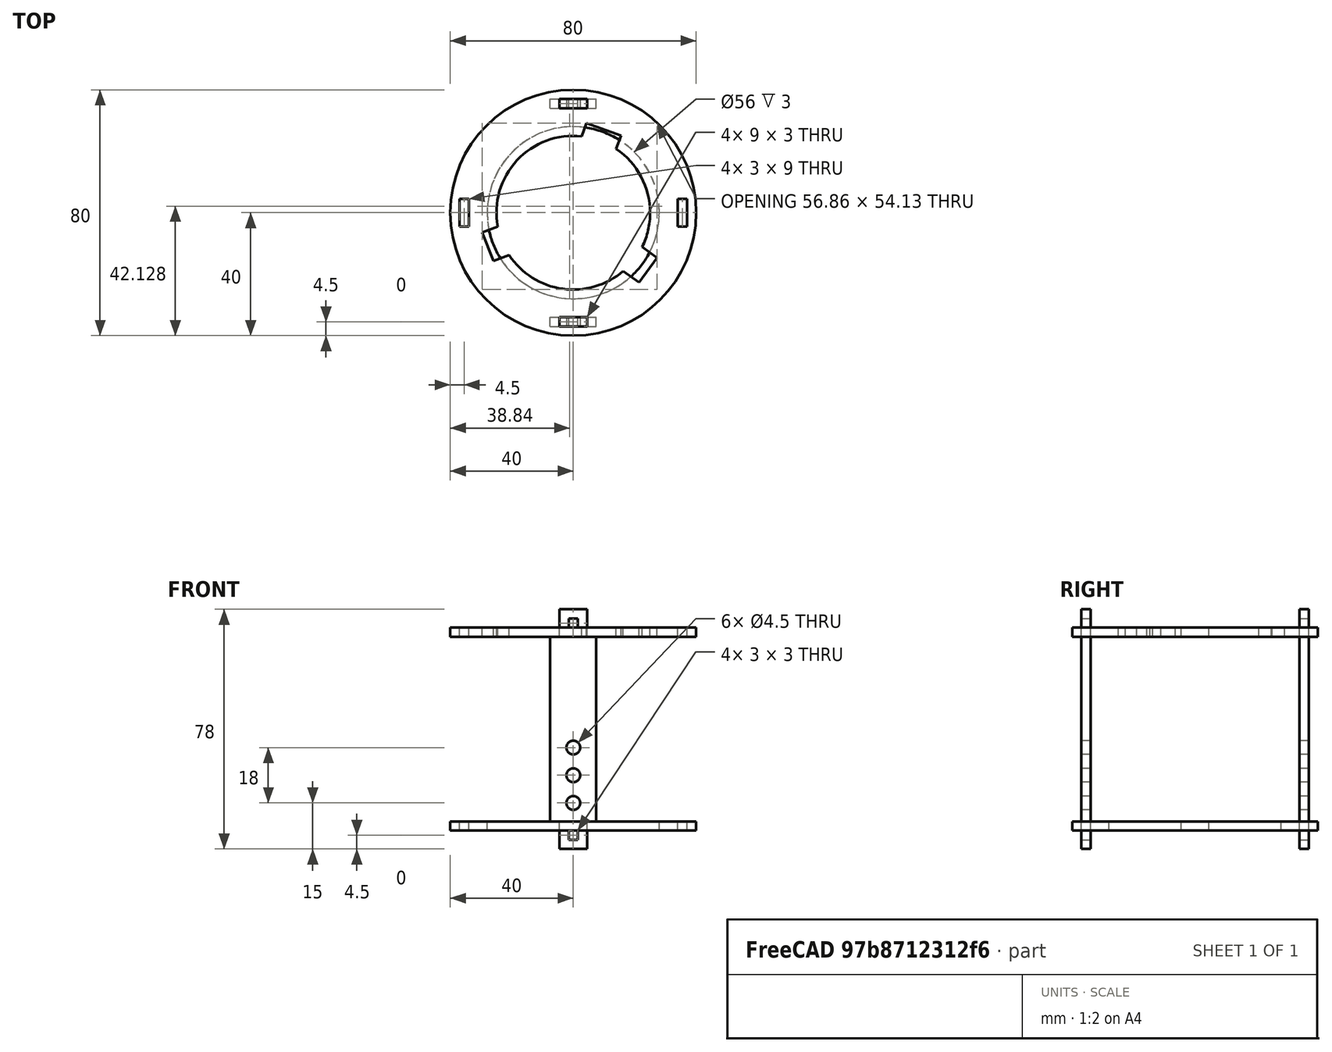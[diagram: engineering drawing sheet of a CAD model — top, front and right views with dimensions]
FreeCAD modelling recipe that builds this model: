
FCSTD DOCUMENT  (FreeCAD 0.16R6707 (Git))
Label: turretPitch
License: All rights reserved
LicenseURL: http://en.wikipedia.org/wiki/All_rights_reserved
objects: Part::Cut×23, Part::Box×21, Part::Cylinder×10, Part::MultiFuse×2
note: 56 computed .brp shape members not serialized (recipe doc carries the construction recipe); baked Part::Feature solids carry a one-line shape summary decoded from their .brp

FEATURE [Part::Cylinder] Cylinder
  Angle = 360
  Height = 3
  Radius = 40
FEATURE [Part::Cylinder] Cylinder001
  Angle = 360
  Height = 3
  Radius = 25
FEATURE [Part::Cut] Cut
  Base = -> Cylinder
  Tool = -> Cylinder001
FEATURE [Part::Box] Box  label="Cube"
  Height = 3
  Length = 3
  Placement = pos=(34,-4.5,0) rot=(0,0,1;0rad)
  Width = 9
FEATURE [Part::Box] Box001  label="Cube001"
  Height = 3
  Length = 3
  Placement = pos=(-37,-4.5,0) rot=(0,0,1;0rad)
  Width = 9
FEATURE [Part::Cut] Cut001
  Base = -> Cut
  Tool = -> Box
FEATURE [Part::Cut] Cut002
  Base = -> Cut001
  Tool = -> Box001
FEATURE [Part::Box] Box002  label="Cube002"
  Height = 3
  Length = 9
  Placement = pos=(-4.5,34,0) rot=(0,0,1;0rad)
  Width = 3
FEATURE [Part::Box] Box003  label="Cube003"
  Height = 3
  Length = 9
  Placement = pos=(-4.5,-37,0) rot=(0,0,1;0rad)
  Width = 3
FEATURE [Part::Cut] Cut003
  Base = -> Cut002
  Tool = -> Box002
FEATURE [Part::Cut] Cut004  label="RingBasis"
  Base = -> Cut003
  Tool = -> Box003
FEATURE [Part::Cylinder] Cylinder002
  Angle = 360
  Height = 3
  Radius = 40
FEATURE [Part::Cylinder] Cylinder003
  Angle = 360
  Height = 3
  Radius = 28
FEATURE [Part::Cut] Cut005
  Base = -> Cylinder002
  Tool = -> Cylinder003
FEATURE [Part::Box] Box004  label="Cube004"
  Height = 3
  Length = 3
  Placement = pos=(34,-4.5,0) rot=(0,0,1;0rad)
  Width = 9
FEATURE [Part::Box] Box005  label="Cube005"
  Height = 3
  Length = 3
  Placement = pos=(-37,-4.5,0) rot=(0,0,1;0rad)
  Width = 9
FEATURE [Part::Cut] Cut006
  Base = -> Cut005
  Tool = -> Box004
FEATURE [Part::Cut] Cut007
  Base = -> Cut006
  Tool = -> Box005
FEATURE [Part::Box] Box006  label="Cube006"
  Height = 3
  Length = 9
  Placement = pos=(-4.5,34,0) rot=(0,0,1;0rad)
  Width = 3
FEATURE [Part::Box] Box007  label="Cube007"
  Height = 3
  Length = 9
  Placement = pos=(-4.5,-37,0) rot=(0,0,1;0rad)
  Width = 3
FEATURE [Part::Cut] Cut008
  Base = -> Cut007
  Tool = -> Box006
FEATURE [Part::Cut] Cut009  label="RingMiddle"
  Base = -> Cut008
  Placement = pos=(0,0,-63) rot=(0,0,1;0rad)
  Tool = -> Box007
FEATURE [Part::Box] Box019  label="Cube019"
  Height = 3
  Length = 12
  Placement = pos=(-6,1,0) rot=(0,0,-1;0.349066rad)
  Width = 30
FEATURE [Part::Box] Box020  label="Cube020"
  Height = 3
  Length = 10
  Placement = pos=(2,-5,0) rot=(0,0,1;1.93731rad)
  Width = 30
FEATURE [Part::Box] Box021  label="Cube021"
  Height = 3
  Length = 10
  Placement = pos=(3,3,0) rot=(0,0,1;4.08407rad)
  Width = 30
FEATURE [Part::Cut] Cut020
  Base = -> Cut004
  Tool = -> Box019
FEATURE [Part::Cut] Cut021
  Base = -> Cut020
  Tool = -> Box021
FEATURE [Part::Cut] Cut022  label="RingBasis001"
  Base = -> Cut021
  Tool = -> Box020
FEATURE [Part::Box] Box009  label="Cube009"
  Height = 9
  Length = 9
  Placement = pos=(-4.5,-66,3) rot=(0,0,1;0rad)
  Width = 3
FEATURE [Part::Box] Box010  label="Cube010"
  Height = 3
  Length = 3
  Placement = pos=(-1.5,-66,6) rot=(0,0,1;0rad)
  Width = 3
FEATURE [Part::Cut] Cut010
  Base = -> Box009
  Placement = pos=(0,0,30) rot=(0,0,1;0rad)
  Tool = -> Box010
FEATURE [Part::Box] Box011  label="Cube011"
  Height = 60
  Length = 15
  Placement = pos=(-7.5,-66,-27) rot=(0,0,1;0rad)
  Width = 3
FEATURE [Part::Box] Box012  label="Cube012"
  Height = 9
  Length = 9
  Placement = pos=(-4.5,-66,3) rot=(0,0,1;0rad)
  Width = 3
FEATURE [Part::Box] Box013  label="Cube013"
  Height = 3
  Length = 3
  Placement = pos=(-1.5,-66,6) rot=(0,0,1;0rad)
  Width = 3
FEATURE [Part::Cut] Cut011
  Base = -> Box012
  Placement = pos=(0,0,-39) rot=(0,0,1;0rad)
  Tool = -> Box013
FEATURE [Part::MultiFuse] Fusion
  Shapes = -> [Cut011,Box011,Cut010]
FEATURE [Part::Cylinder] Cylinder004
  Angle = 360
  Height = 3
  Placement = pos=(0,-63,-12) rot=(1,0,0;1.5708rad)
  Radius = 2.25
FEATURE [Part::Cylinder] Cylinder005
  Angle = 360
  Height = 3
  Placement = pos=(0,-63,-3) rot=(1,0,0;1.5708rad)
  Radius = 2.25
FEATURE [Part::Cylinder] Cylinder006
  Angle = 360
  Height = 3
  Placement = pos=(0,-63,-21) rot=(1,0,0;1.5708rad)
  Radius = 2.25
FEATURE [Part::Cut] Cut012
  Base = -> Fusion
  Tool = -> Cylinder004
FEATURE [Part::Cut] Cut013
  Base = -> Cut012
  Tool = -> Cylinder006
FEATURE [Part::Cut] Cut014  label="pitchRingConnector"
  Base = -> Cut013
  Placement = pos=(0,29,-33) rot=(0,0,1;0rad)
  Tool = -> Cylinder005
FEATURE [Part::Box] Box022  label="Cube022"
  Height = 9
  Length = 9
  Placement = pos=(-4.5,-66,3) rot=(0,0,1;0rad)
  Width = 3
FEATURE [Part::Box] Box023  label="Cube023"
  Height = 3
  Length = 3
  Placement = pos=(-1.5,-66,6) rot=(0,0,1;0rad)
  Width = 3
FEATURE [Part::Cut] Cut023
  Base = -> Box022
  Placement = pos=(0,0,30) rot=(0,0,1;0rad)
  Tool = -> Box023
FEATURE [Part::Box] Box024  label="Cube024"
  Height = 60
  Length = 15
  Placement = pos=(-7.5,-66,-27) rot=(0,0,1;0rad)
  Width = 3
FEATURE [Part::Box] Box025  label="Cube025"
  Height = 9
  Length = 9
  Placement = pos=(-4.5,-66,3) rot=(0,0,1;0rad)
  Width = 3
FEATURE [Part::Box] Box026  label="Cube026"
  Height = 3
  Length = 3
  Placement = pos=(-1.5,-66,6) rot=(0,0,1;0rad)
  Width = 3
FEATURE [Part::Cut] Cut024
  Base = -> Box025
  Placement = pos=(0,0,-39) rot=(0,0,1;0rad)
  Tool = -> Box026
FEATURE [Part::MultiFuse] Fusion001
  Shapes = -> [Cut024,Box024,Cut023]
FEATURE [Part::Cylinder] Cylinder007
  Angle = 360
  Height = 3
  Placement = pos=(0,-63,-12) rot=(1,0,0;1.5708rad)
  Radius = 2.25
FEATURE [Part::Cylinder] Cylinder008
  Angle = 360
  Height = 3
  Placement = pos=(0,-63,-3) rot=(1,0,0;1.5708rad)
  Radius = 2.25
FEATURE [Part::Cylinder] Cylinder009
  Angle = 360
  Height = 3
  Placement = pos=(0,-63,-21) rot=(1,0,0;1.5708rad)
  Radius = 2.25
FEATURE [Part::Cut] Cut025
  Base = -> Fusion001
  Tool = -> Cylinder007
FEATURE [Part::Cut] Cut026
  Base = -> Cut025
  Tool = -> Cylinder009
FEATURE [Part::Cut] Cut027  label="pitchRingConnector001"
  Base = -> Cut026
  Placement = pos=(0,100,-33) rot=(0,0,1;0rad)
  Tool = -> Cylinder008
